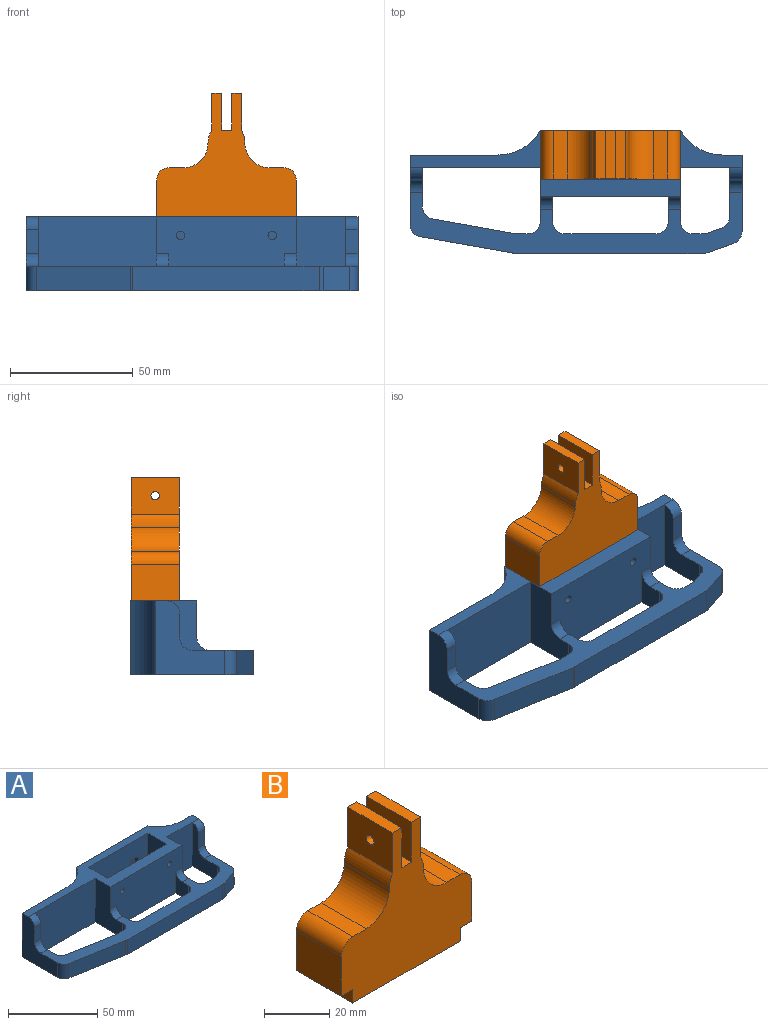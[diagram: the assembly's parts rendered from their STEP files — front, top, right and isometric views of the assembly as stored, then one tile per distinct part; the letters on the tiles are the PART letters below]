
ASSEMBLY  parts=2 mates=1
PART A: 67 faces, bbox 135x50x30 mm
  f0: plane 47x30mm, normal (0,-1,0), area 1336.9mm2, adj f17,f18,f20,f32,f35,f36,f37,f38
  f1: cylinder r=1.75mm len=3.5mm, axis (0,-1,0), area 22mm2, adj f16,f48
  f2: cylinder r=1.75mm len=3.5mm, axis (0,-1,0), area 22mm2, adj f16,f41
  f3: plane 35.68x30mm, normal (0,1,0), area 1070.4mm2, adj f4,f20,f32,f66
  f4: plane 30x28.22mm, normal (-1,0,0), area 482.2mm2, adj f3,f5,f20,f31,f32,f51,f61,f64
  f5: plane 10x5mm, normal (0,-1,0), area 50mm2, adj f4,f6,f61,f64
  f6: plane 30x15.99mm, normal (1,0,0), area 259.9mm2, adj f5,f7,f20,f31,f50,f61,f64
  f7: plane 48x30mm, normal (0,-1,0), area 1440mm2, adj f6,f8,f20,f32
  f8: plane 30x22mm, normal (-1,0,0), area 465.4mm2, adj f7,f9,f20,f31,f32,f49,f62
  f9: plane 57x30mm, normal (0,-1,0), area 1540.8mm2, adj f8,f10,f20,f21,f29,f32,f33,f34
  f10: plane 30x22mm, normal (1,0,0), area 465.4mm2, adj f9,f11,f20,f31,f32,f56,f59
  f11: plane 30x20mm, normal (0,-1,0), area 600mm2, adj f10,f12,f20,f32
  f12: plane 30x19.95mm, normal (-1,0,0), area 299.5mm2, adj f11,f13,f20,f31,f55,f60,f63
  f13: plane 10x5mm, normal (0,-1,0), area 50mm2, adj f12,f14,f60,f63
  f14: plane 31.19x30mm, normal (1,0,0), area 511.9mm2, adj f13,f15,f20,f31,f32,f54,f60,f63
  f15: plane 30x7.68mm, normal (0,1,0), area 230.4mm2, adj f14,f20,f32,f65
  f16: plane 57x30mm, normal (0,1,0), area 1690.8mm2, adj f1,f2,f20,f32,f65,f66
  f17: plane 30x15mm, normal (1,0,0), area 450mm2, adj f0,f19,f20,f32
  f18: plane 30x15mm, normal (-1,0,0), area 450mm2, adj f0,f19,f20,f32
  f19: plane 47x30mm, normal (0,1,0), area 1390.8mm2, adj f17,f18,f20,f32,f33,f34
  f20: plane 135x50mm, normal (0,0,-1), area 2790.8mm2, adj f0,f3,f4,f6,f7,f8,f9,f10
  f21: plane 15x10mm, normal (1,0,0), area 105.4mm2, adj f9,f20,f31,f58,f62
  f22: plane 10x5mm, normal (0,1,0), area 50mm2, adj f20,f23,f31,f49
  f23: plane 33.88x10mm, normal (0.18,0.98,0), area 344.3mm2, adj f20,f22,f31,f50
  f24: plane 38.44x10mm, normal (-0.17,-0.98,0), area 390.3mm2, adj f20,f31,f51,f52
  f25: plane 75.71x10mm, normal (0,-1,0), area 757.1mm2, adj f20,f31,f52,f53
  f26: plane 10.85x10mm, normal (0.33,-0.94,0), area 115mm2, adj f20,f31,f53,f54
  f27: plane 10x6.66mm, normal (-0.33,0.94,0), area 70.5mm2, adj f20,f28,f31,f55
  f28: plane 10x5mm, normal (0,1,0), area 50mm2, adj f20,f27,f31,f56
  f29: plane 15x10mm, normal (-1,0,0), area 105.4mm2, adj f9,f20,f31,f57,f59
  f30: plane 37x10mm, normal (0,1,0), area 370mm2, adj f20,f31,f57,f58
  f31: plane 135x25mm, normal (0,0,1), area 1316.1mm2, adj f4,f6,f8,f10,f12,f14,f21,f22
  f32: plane 135x27mm, normal (0,0,1), area 1324.7mm2, adj f0,f3,f4,f7,f8,f9,f10,f11
  f33: cylinder r=1.75mm len=7mm, axis (0,-1,0), area 77mm2, adj f9,f19
  f34: cylinder r=1.75mm len=7mm, axis (0,-1,0), area 77mm2, adj f9,f19
  f35: plane 3.25x3mm, normal (-0.5,0,-0.87), area 11.2mm2, adj f0,f36,f40,f41
  f36: plane 3.25x3mm, normal (0.5,0,-0.87), area 11.2mm2, adj f0,f35,f37,f41
  f37: plane 3.75x3mm, normal (1,0,0), area 11.3mm2, adj f0,f36,f38,f41
  f38: plane 3.25x3mm, normal (0.5,0,0.87), area 11.2mm2, adj f0,f37,f39,f41
  f39: plane 3.25x3mm, normal (-0.5,0,0.87), area 11.2mm2, adj f0,f38,f40,f41
  f40: plane 3.75x3mm, normal (-1,0,0), area 11.3mm2, adj f0,f35,f39,f41
  f41: plane 7.5x6.5mm, normal (0,-1,0), area 26.9mm2, adj f2,f35,f36,f37,f38,f39,f40
  f42: plane 3.25x3mm, normal (-0.5,0,-0.87), area 11.2mm2, adj f0,f43,f47,f48
  f43: plane 3.25x3mm, normal (0.5,0,-0.87), area 11.2mm2, adj f0,f42,f44,f48
  f44: plane 3.75x3mm, normal (1,0,0), area 11.3mm2, adj f0,f43,f45,f48
  f45: plane 3.25x3mm, normal (0.5,0,0.87), area 11.2mm2, adj f0,f44,f46,f48
  f46: plane 3.25x3mm, normal (-0.5,0,0.87), area 11.2mm2, adj f0,f45,f47,f48
  f47: plane 3.75x3mm, normal (-1,0,0), area 11.3mm2, adj f0,f42,f46,f48
  f48: plane 7.5x6.5mm, normal (0,-1,0), area 26.9mm2, adj f1,f42,f43,f44,f45,f46,f47
  f49: cylinder r=5mm len=10mm, axis (0,0,-1), area 78.5mm2, adj f8,f20,f22,f31
  f50: cylinder r=5mm len=10mm, axis (0,0,1), area 69.7mm2, adj f6,f20,f23,f31
  f51: cylinder r=5mm len=10mm, axis (0,0,1), area 69.8mm2, adj f4,f20,f24,f31
  f52: cylinder r=5mm len=10mm, axis (0,0,1), area 8.7mm2, adj f20,f24,f25,f31
  f53: cylinder r=5mm len=10mm, axis (0,0,-1), area 16.9mm2, adj f20,f25,f26,f31
  f54: cylinder r=5mm len=10mm, axis (0,0,1), area 61.7mm2, adj f14,f20,f26,f31
  f55: cylinder r=5mm len=10mm, axis (0,0,-1), area 61.7mm2, adj f12,f20,f27,f31
  f56: cylinder r=5mm len=10mm, axis (0,0,1), area 78.5mm2, adj f10,f20,f28,f31
  f57: cylinder r=5mm len=10mm, axis (0,0,1), area 78.5mm2, adj f20,f29,f30,f31
  f58: cylinder r=5mm len=10mm, axis (0,0,-1), area 78.5mm2, adj f20,f21,f30,f31
  f59: cylinder r=5mm len=5mm, axis (-1,0,0), area 39.3mm2, adj f9,f10,f29,f31
  f60: cylinder r=5mm len=5mm, axis (1,0,0), area 39.3mm2, adj f12,f13,f14,f31
  f61: cylinder r=5mm len=5mm, axis (1,0,0), area 39.3mm2, adj f4,f5,f6,f31
  f62: cylinder r=5mm len=5mm, axis (1,0,0), area 39.3mm2, adj f8,f9,f21,f31
  f63: cylinder r=5mm len=5mm, axis (-1,0,0), area 39.3mm2, adj f12,f13,f14,f32
  f64: cylinder r=5mm len=5mm, axis (-1,0,0), area 39.3mm2, adj f4,f5,f6,f32
  f65: cylinder r=20mm len=30mm, axis (0,0,1), area 628.3mm2, adj f15,f16,f20,f32
  f66: cylinder r=20mm len=30mm, axis (0,0,1), area 628.3mm2, adj f3,f16,f20,f32
PART B: 26 faces, bbox 56.7x19.6x55.3 mm
  f0: plane 19.56x4.16mm, normal (0,0,1), area 81.3mm2, adj f2,f9,f12,f15
  f1: plane 19.56x5.85mm, normal (0,0,1), area 114.4mm2, adj f2,f9,f21,f25
  f2: plane 56.7x55.3mm, normal (0,-1,0), area 1744.2mm2, adj f0,f1,f3,f5,f6,f7,f8,f10
  f3: plane 14.56x5mm, normal (1,0,0), area 72.8mm2, adj f2,f4,f6,f11
  f4: plane 46.7x5mm, normal (0,1,0), area 233.5mm2, adj f3,f5,f6,f11
  f5: plane 14.56x5mm, normal (-1,0,0), area 72.8mm2, adj f2,f4,f6,f11
  f6: plane 46.7x14.56mm, normal (0,0,-1), area 680mm2, adj f2,f3,f4,f5
  f7: plane 19.56x15mm, normal (-1,0,0), area 293.4mm2, adj f2,f9,f11,f25
  f8: plane 19.56x15mm, normal (1,0,0), area 293.4mm2, adj f2,f9,f11,f24
  f9: plane 56.7x50.3mm, normal (0,1,0), area 1510.7mm2, adj f0,f1,f7,f8,f10,f11,f12,f13
  f10: plane 19.56x5.85mm, normal (0,0,1), area 114.4mm2, adj f2,f9,f20,f24
  f11: plane 56.7x19.56mm, normal (0,0,-1), area 429.1mm2, adj f2,f3,f4,f5,f7,f8,f9
  f12: plane 19.56x15mm, normal (1,0,0), area 284.3mm2, adj f0,f2,f9,f14,f19
  f13: plane 19.56x15mm, normal (-1,0,0), area 284.3mm2, adj f2,f9,f14,f19,f22
  f14: plane 19.56x4mm, normal (0,0,1), area 78.2mm2, adj f2,f9,f12,f13
  f15: plane 19.56x15mm, normal (-1,0,0), area 284.3mm2, adj f0,f2,f9,f17,f18
  f16: plane 19.56x15mm, normal (1,0,0), area 284.3mm2, adj f2,f9,f17,f18,f23
  f17: plane 19.56x4mm, normal (0,0,1), area 78.2mm2, adj f2,f9,f15,f16
  f18: cylinder r=1.7mm len=4mm, axis (-1,0,0), area 42.7mm2, adj f15,f16
  f19: cylinder r=1.7mm len=4mm, axis (-1,0,0), area 42.7mm2, adj f12,f13
  f20: cylinder r=10mm len=19.56mm, axis (0,1,0), area 306.8mm2, adj f2,f9,f10,f23
  f21: cylinder r=10mm len=19.56mm, axis (0,-1,0), area 305.3mm2, adj f1,f2,f9,f22
  f22: cylinder r=10.86mm len=19.56mm, axis (0,1,0), area 110.9mm2, adj f2,f9,f13,f21
  f23: cylinder r=11.35mm len=19.56mm, axis (0,1,0), area 108.5mm2, adj f2,f9,f16,f20
  f24: cylinder r=5mm len=19.56mm, axis (0,-1,0), area 153.6mm2, adj f2,f8,f9,f10
  f25: cylinder r=5mm len=19.56mm, axis (0,1,0), area 153.6mm2, adj f1,f2,f7,f9
PLACE A t=(9.41,4.65,-15.21)mm fixed
PLACE B t=(9.41,4.65,14.79)mm
MATE slider B.f6 <-> A.f32  axis (0,0,-1) through (9.41,4.65,9.79)mm
